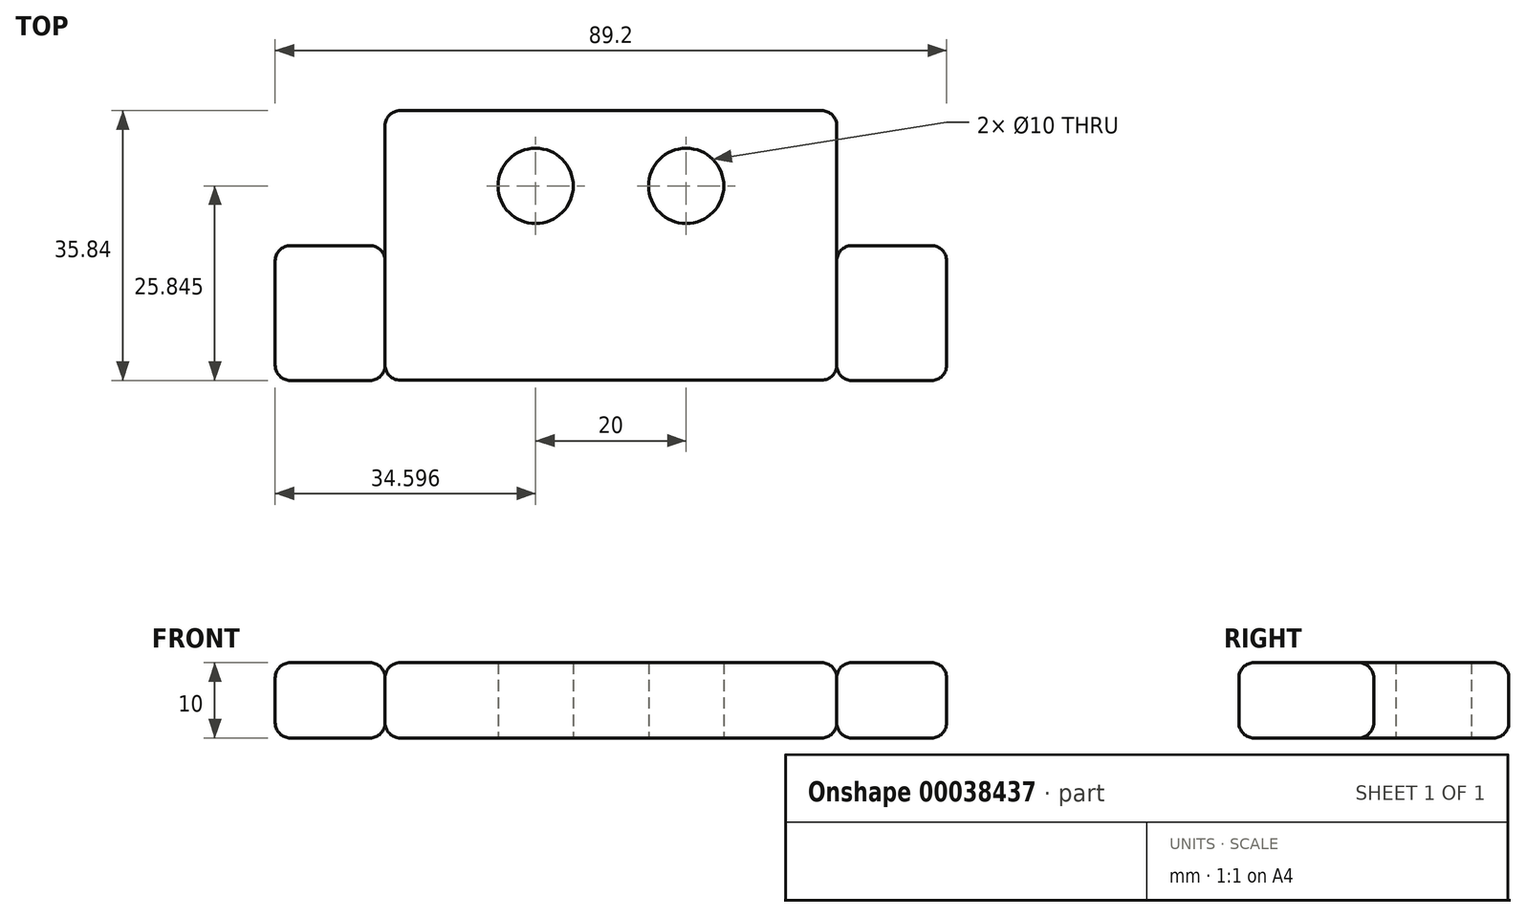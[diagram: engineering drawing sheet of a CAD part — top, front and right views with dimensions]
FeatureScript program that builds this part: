
annotation { "Feature Type Name" : "Feature", "Feature Type Description" : "" }
export const myFeature = defineFeature(function(context is Context, id is Id, definition is map)
    precondition{}
    {
        {
            var Q0;
            Q0=qCreatedBy(makeId("Top.planeOp"),FACE);
            var sketch = newSketch(context, id + "F0", { "sketchPlane" : qUnion([Q0])});
            skLineSegment(sketch, "E0.bottom", {"start": v(-48.67, 16.73) * mm, "end": v(11.33, 16.73) * mm});
            skLineSegment(sketch, "E0.top", {"start": v(-48.67, -19.07) * mm, "end": v(11.33, -19.07) * mm});
            skLineSegment(sketch, "E0.left", {"start": v(-48.67, 16.73) * mm, "end": v(-48.67, -19.07) * mm});
            skLineSegment(sketch, "E0.right", {"start": v(11.33, 16.73) * mm, "end": v(11.33, -19.07) * mm});
            skLineSegment(sketch, "E1.bottom", {"start": v(-48.67, -1.21) * mm, "end": v(-63.27, -1.21) * mm});
            skLineSegment(sketch, "E1.top", {"start": v(-48.67, -19.11) * mm, "end": v(-63.27, -19.11) * mm});
            skLineSegment(sketch, "E1.left", {"start": v(-48.67, -1.21) * mm, "end": v(-48.67, -19.11) * mm});
            skLineSegment(sketch, "E1.right", {"start": v(-63.27, -1.21) * mm, "end": v(-63.27, -19.11) * mm});
            skLineSegment(sketch, "E2.bottom", {"start": v(11.33, -1.21) * mm, "end": v(25.93, -1.21) * mm});
            skLineSegment(sketch, "E2.top", {"start": v(11.33, -19.11) * mm, "end": v(25.93, -19.11) * mm});
            skLineSegment(sketch, "E2.left", {"start": v(11.33, -1.21) * mm, "end": v(11.33, -19.11) * mm});
            skLineSegment(sketch, "E2.right", {"start": v(25.93, -1.21) * mm, "end": v(25.93, -19.11) * mm});
            skCircle(sketch, "E3", {"center": v(-28.67, 6.73) * mm, "radius": 5 * mm});
            skCircle(sketch, "E4", {"center": v(-8.67, 6.73) * mm, "radius": 5 * mm});
            skLineSegment(sketch, "E5", {"start": v(-28.67, 6.73) * mm, "end": v(-28.67, 16.73) * mm, "construction": true});
            skSolve(sketch);
        }
        {
            var Q0;
            Q0=makeQuery(id+"F0.imprint","IMPRINT",FACE,{"disambiguationData":[TD([[makeQuery(id+"F0.imprint","IMPRINT",EDGE,{"derivedFrom":sQuery(id+"F0.wireOp",EDGE,"E1.bottom")}),1.0]])]});
            var Q1;
            Q1=makeQuery(id+"F0.imprint","IMPRINT",FACE,{"disambiguationData":[TD([[makeQuery(id+"F0.imprint","IMPRINT",EDGE,{"derivedFrom":sQuery(id+"F0.wireOp",EDGE,"E2.bottom")}),-1.0]])]});
            extrude(context, id + "F1", {"entities" : qUnion([Q0, Q1]), "depth" : 10 * mm});
        }
        {
            var Q0;
            Q0=makeQuery(id+"F0.imprint","IMPRINT",FACE,{"disambiguationData":[TD([[makeQuery(id+"F0.imprint","IMPRINT",EDGE,{"derivedFrom":sQuery(id+"F0.wireOp",EDGE,"E0.bottom")}),-1.0]])]});
            extrude(context, id + "F2", {"entities" : qUnion([Q0]), "depth" : 10 * mm});
        }
        {
            var Q0;
            Q0=makeQuery(id+"F2.opExtrude","CAP_EDGE",EDGE,{"disambiguationData":[OSD([sQuery(id+"F0.wireOp",EDGE,"E0.bottom")])],"isStart":false});
            var Q1;
            Q1=makeQuery(id+"F2.opExtrude","CAP_EDGE",EDGE,{"disambiguationData":[OSD([sQuery(id+"F0.wireOp",EDGE,"E0.right"),sQuery(id+"F0.wireOp",EDGE,"E2.left")])],"isStart":false});
            var Q2;
            Q2=makeQuery(id+"F2.opExtrude","CAP_EDGE",EDGE,{"disambiguationData":[OSD([sQuery(id+"F0.wireOp",EDGE,"E0.left"),sQuery(id+"F0.wireOp",EDGE,"E1.left")])],"isStart":false});
            var Q3;
            Q3=makeQuery(id+"F1.opExtrude","CAP_EDGE",EDGE,{"disambiguationData":[OSD([sQuery(id+"F0.wireOp",EDGE,"E1.right")])],"isStart":false});
            var Q4;
            Q4=makeQuery(id+"F1.opExtrude","CAP_EDGE",EDGE,{"disambiguationData":[OSD([sQuery(id+"F0.wireOp",EDGE,"E1.top")])],"isStart":false});
            var Q5;
            Q5=makeQuery(id+"F2.opExtrude","CAP_EDGE",EDGE,{"disambiguationData":[OSD([sQuery(id+"F0.wireOp",EDGE,"E0.top")])],"isStart":false});
            var Q6;
            Q6=makeQuery(id+"F1.opExtrude","CAP_EDGE",EDGE,{"disambiguationData":[OSD([sQuery(id+"F0.wireOp",EDGE,"E2.top")])],"isStart":false});
            var Q7;
            Q7=makeQuery(id+"F1.opExtrude","CAP_EDGE",EDGE,{"disambiguationData":[OSD([sQuery(id+"F0.wireOp",EDGE,"E2.bottom")])],"isStart":false});
            var Q8;
            Q8=makeQuery(id+"F1.opExtrude","CAP_EDGE",EDGE,{"disambiguationData":[OSD([sQuery(id+"F0.wireOp",EDGE,"E2.right")])],"isStart":false});
            var Q9;
            Q9=makeQuery(id+"F1.opExtrude","CAP_EDGE",EDGE,{"disambiguationData":[OSD([sQuery(id+"F0.wireOp",EDGE,"E2.right")])],"isStart":true});
            var Q10;
            Q10=makeQuery(id+"F1.opExtrude","SWEPT_EDGE",EDGE,{"disambiguationData":[OSD([sQuery(id+"F0.wireOp",EDGE,"E2.bottom"),sQuery(id+"F0.wireOp",EDGE,"E2.right")])]});
            var Q11;
            Q11=makeQuery(id+"F1.opExtrude","CAP_EDGE",EDGE,{"disambiguationData":[OSD([sQuery(id+"F0.wireOp",EDGE,"E2.bottom")])],"isStart":true});
            var Q12;
            Q12=makeQuery(id+"F2.opExtrude","SWEPT_EDGE",EDGE,{"disambiguationData":[OSD([sQuery(id+"F0.wireOp",EDGE,"E0.bottom"),sQuery(id+"F0.wireOp",EDGE,"E0.right")])]});
            var Q13;
            Q13=makeQuery(id+"F2.opExtrude","SWEPT_EDGE",EDGE,{"disambiguationData":[OSD([sQuery(id+"F0.wireOp",EDGE,"E0.bottom"),sQuery(id+"F0.wireOp",EDGE,"E0.left")])]});
            var Q14;
            Q14=makeQuery(id+"F1.opExtrude","CAP_EDGE",EDGE,{"disambiguationData":[OSD([sQuery(id+"F0.wireOp",EDGE,"E1.bottom")])],"isStart":true});
            var Q15;
            Q15=makeQuery(id+"F2.opExtrude","CAP_EDGE",EDGE,{"disambiguationData":[OSD([sQuery(id+"F0.wireOp",EDGE,"E0.top")])],"isStart":true});
            var Q16;
            Q16=makeQuery(id+"F1.opExtrude","CAP_EDGE",EDGE,{"disambiguationData":[OSD([sQuery(id+"F0.wireOp",EDGE,"E2.left")])],"isStart":true});
            var Q17;
            Q17=makeQuery(id+"F1.opExtrude","CAP_EDGE",EDGE,{"disambiguationData":[OSD([sQuery(id+"F0.wireOp",EDGE,"E1.left")])],"isStart":true});
            var Q18;
            Q18=makeQuery(id+"F2.opExtrude","CAP_EDGE",EDGE,{"disambiguationData":[OSD([sQuery(id+"F0.wireOp",EDGE,"E0.bottom")])],"isStart":true});
            var Q19;
            Q19=makeQuery(id+"F1.opExtrude","SWEPT_EDGE",EDGE,{"disambiguationData":[OSD([sQuery(id+"F0.wireOp",EDGE,"E2.top"),sQuery(id+"F0.wireOp",EDGE,"E2.right")])]});
            var Q20;
            Q20=makeQuery(id+"F1.opExtrude","CAP_EDGE",EDGE,{"disambiguationData":[OSD([sQuery(id+"F0.wireOp",EDGE,"E2.top")])],"isStart":true});
            var Q21;
            Q21=makeQuery(id+"F2.opExtrude","SWEPT_EDGE",EDGE,{"disambiguationData":[OSD([sQuery(id+"F0.wireOp",EDGE,"E0.top"),sQuery(id+"F0.wireOp",EDGE,"E0.left")])]});
            var Q22;
            Q22=makeQuery(id+"F1.opExtrude","CAP_EDGE",EDGE,{"disambiguationData":[OSD([sQuery(id+"F0.wireOp",EDGE,"E1.top")])],"isStart":true});
            var Q23;
            Q23=makeQuery(id+"F1.opExtrude","SWEPT_EDGE",EDGE,{"disambiguationData":[OSD([sQuery(id+"F0.wireOp",EDGE,"E1.top"),sQuery(id+"F0.wireOp",EDGE,"E1.right")])]});
            var Q24;
            Q24=makeQuery(id+"F1.opExtrude","SWEPT_EDGE",EDGE,{"disambiguationData":[OSD([sQuery(id+"F0.wireOp",EDGE,"E1.bottom"),sQuery(id+"F0.wireOp",EDGE,"E1.right")])]});
            var Q25;
            Q25=makeQuery(id+"F2.opExtrude","SWEPT_FACE",FACE,{"disambiguationData":[OSD([sQuery(id+"F0.wireOp",EDGE,"E0.left"),sQuery(id+"F0.wireOp",EDGE,"E1.left")])]});
            var Q26;
            Q26=makeQuery(id+"F2.opExtrude","SWEPT_FACE",FACE,{"disambiguationData":[OSD([sQuery(id+"F0.wireOp",EDGE,"E0.right"),sQuery(id+"F0.wireOp",EDGE,"E2.left")])]});
            var Q27;
            Q27=makeQuery(id+"F1.opExtrude","CAP_EDGE",EDGE,{"disambiguationData":[OSD([sQuery(id+"F0.wireOp",EDGE,"E1.right")])],"isStart":true});
            fillet(context, id + "F3", {"entities" : qUnion([Q0, Q1, Q2, Q3, Q4, Q5, Q6, Q7, Q8, Q9, Q10, Q11, Q12, Q13, Q14, Q15, Q16, Q17, Q18, Q19, Q20, Q21, Q22, Q23, Q24, Q25, Q26, Q27]), "radius" : 2 * mm, "tangentPropagation" : true, "allowEdgeOverflow" : false});
        }
        {
            var Q0;
            Q0=makeQuery(id+"F1.opExtrude","SWEPT_EDGE",EDGE,{"disambiguationData":[OSD([sQuery(id+"F0.wireOp",EDGE,"E0.left"),sQuery(id+"F0.wireOp",EDGE,"E1.bottom"),sQuery(id+"F0.wireOp",EDGE,"E1.left")])]});
            var Q1;
            {var subQ0=sQuery(id+"F0.wireOp",EDGE,"E2.bottom");Q1=makeQuery(id+"F3.opFillet","BLEND_EDGE",EDGE,{"blendedFrom":[makeQuery(id+"F1.opExtrude","CAP_EDGE",EDGE,{"disambiguationData":[OSD([subQ0])],"isStart":false}),makeQuery(id+"F1.opExtrude","CAP_FACE",FACE,{"disambiguationData":[OSD([subQ0,sQuery(id+"F0.wireOp",EDGE,"E2.top"),sQuery(id+"F0.wireOp",EDGE,"E2.left"),sQuery(id+"F0.wireOp",EDGE,"E2.right")])],"isStart":false})],"blendedInto":[makeQuery(id+"F1.opExtrude","CAP_FACE",FACE,{"disambiguationData":[OSD([subQ0,sQuery(id+"F0.wireOp",EDGE,"E2.top"),sQuery(id+"F0.wireOp",EDGE,"E2.left"),sQuery(id+"F0.wireOp",EDGE,"E2.right")])],"isStart":false})]});}
            var Q2;
            Q2=makeQuery(id+"F3.opFillet","BLEND_EDGE",EDGE,{"blendedFrom":[makeQuery(id+"F1.opExtrude","CAP_EDGE",EDGE,{"disambiguationData":[OSD([sQuery(id+"F0.wireOp",EDGE,"E2.bottom")])],"isStart":false}),makeQuery(id+"F1.opExtrude","SWEPT_FACE",FACE,{"disambiguationData":[OSD([sQuery(id+"F0.wireOp",EDGE,"E2.left")])]})],"blendedInto":[makeQuery(id+"F1.opExtrude","SWEPT_FACE",FACE,{"disambiguationData":[OSD([sQuery(id+"F0.wireOp",EDGE,"E2.left")])]})]});
            var Q3;
            Q3=makeQuery(id+"F1.opExtrude","CAP_EDGE",EDGE,{"disambiguationData":[OSD([sQuery(id+"F0.wireOp",EDGE,"E1.bottom")])],"isStart":false});
            fillet(context, id + "F4", {"entities" : qUnion([Q0, Q1, Q2, Q3]), "radius" : 2 * mm, "tangentPropagation" : true, "allowEdgeOverflow" : false});
        }
        {
            var Q0;
            {var subQ0=sQuery(id+"F0.wireOp",EDGE,"E0.top");var subQ1=sQuery(id+"F0.wireOp",EDGE,"E0.left");Q0=makeQuery(id+"F3.opFillet","BLEND_EDGE",EDGE,{"blendedFrom":[makeQuery(id+"F2.opExtrude","CAP_VERTEX",VERTEX,{"disambiguationData":[OSD([subQ0,subQ1])],"isStart":false}),makeQuery(id+"F2.opExtrude","SWEPT_EDGE",EDGE,{"disambiguationData":[OSD([subQ0,subQ1])]})],"blendedInto":[]});}
            var Q1;
            Q1=makeQuery(id+"F3.opFillet","BLEND_EDGE",EDGE,{"blendedFrom":[makeQuery(id+"F1.opExtrude","CAP_EDGE",EDGE,{"disambiguationData":[OSD([sQuery(id+"F0.wireOp",EDGE,"E1.top")])],"isStart":false}),makeQuery(id+"F1.opExtrude","SWEPT_FACE",FACE,{"disambiguationData":[OSD([sQuery(id+"F0.wireOp",EDGE,"E1.left")])]})],"blendedInto":[makeQuery(id+"F1.opExtrude","SWEPT_FACE",FACE,{"disambiguationData":[OSD([sQuery(id+"F0.wireOp",EDGE,"E1.left")])]})]});
            fillet(context, id + "F5", {"entities" : qUnion([Q0, Q1]), "radius" : 2 * mm, "tangentPropagation" : true, "allowEdgeOverflow" : false});
        }
    });
